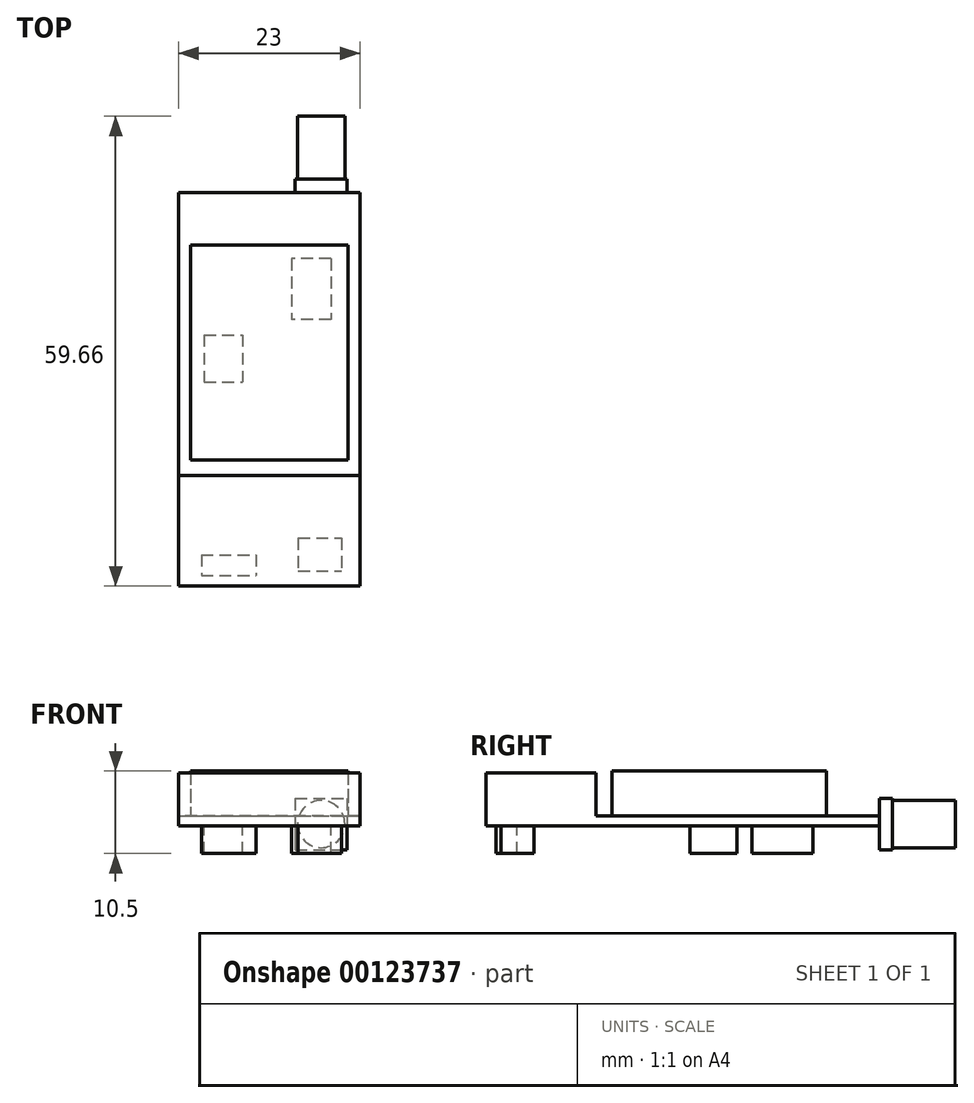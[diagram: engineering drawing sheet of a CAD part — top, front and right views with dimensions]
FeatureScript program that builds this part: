
annotation { "Feature Type Name" : "Feature", "Feature Type Description" : "" }
export const myFeature = defineFeature(function(context is Context, id is Id, definition is map)
    precondition{}
    {
        {
            var Q0;
            Q0=qCreatedBy(makeId("Top.planeOp"),FACE);
            var sketch = newSketch(context, id + "F0", { "sketchPlane" : qUnion([Q0])});
            skLineSegment(sketch, "E0.bottom", {"start": v(-11.5, 25) * mm, "end": v(11.5, 25) * mm});
            skLineSegment(sketch, "E0.top", {"start": v(-11.5, -25) * mm, "end": v(11.5, -25) * mm});
            skLineSegment(sketch, "E0.left", {"start": v(-11.5, 25) * mm, "end": v(-11.5, -25) * mm});
            skLineSegment(sketch, "E0.right", {"start": v(11.5, 25) * mm, "end": v(11.5, -25) * mm});
            skPoint(sketch, "E0.middle", {"position": v(0, 0) * mm});
            skLineSegment(sketch, "E1.bottom", {"start": v(-10, 18.3) * mm, "end": v(10, 18.3) * mm});
            skLineSegment(sketch, "E1.top", {"start": v(-10, -9) * mm, "end": v(10, -9) * mm});
            skLineSegment(sketch, "E1.left", {"start": v(-10, 18.3) * mm, "end": v(-10, -9) * mm});
            skLineSegment(sketch, "E1.right", {"start": v(10, 18.3) * mm, "end": v(10, -9) * mm});
            skPoint(sketch, "E1.middle", {"position": v(0, 4.65) * mm});
            skLineSegment(sketch, "E2", {"start": v(-11.5, -11) * mm, "end": v(11.5, -11) * mm});
            skLineSegment(sketch, "E3", {"start": v(3.3, 25) * mm, "end": v(3.3, 26.66) * mm});
            skLineSegment(sketch, "E4", {"start": v(3.3, 26.66) * mm, "end": v(9.9, 26.66) * mm});
            skLineSegment(sketch, "E5", {"start": v(9.9, 26.66) * mm, "end": v(9.9, 25) * mm});
            skLineSegment(sketch, "E6.bottom", {"start": v(7.85, 16.58) * mm, "end": v(2.83, 16.58) * mm});
            skLineSegment(sketch, "E6.top", {"start": v(7.85, 8.82) * mm, "end": v(2.83, 8.82) * mm});
            skLineSegment(sketch, "E6.left", {"start": v(7.85, 16.58) * mm, "end": v(7.85, 8.82) * mm});
            skLineSegment(sketch, "E6.right", {"start": v(2.83, 16.58) * mm, "end": v(2.83, 8.82) * mm});
            skLineSegment(sketch, "E7.bottom", {"start": v(-8.28, 6.9) * mm, "end": v(-3.38, 6.9) * mm});
            skLineSegment(sketch, "E7.top", {"start": v(-8.28, 0.93) * mm, "end": v(-3.38, 0.93) * mm});
            skLineSegment(sketch, "E7.left", {"start": v(-8.28, 6.9) * mm, "end": v(-8.28, 0.93) * mm});
            skLineSegment(sketch, "E7.right", {"start": v(-3.38, 6.9) * mm, "end": v(-3.38, 0.93) * mm});
            skLineSegment(sketch, "E8.bottom", {"start": v(-8.64, -21.05) * mm, "end": v(-1.7, -21.05) * mm});
            skLineSegment(sketch, "E8.top", {"start": v(-8.64, -23.68) * mm, "end": v(-1.7, -23.68) * mm});
            skLineSegment(sketch, "E8.left", {"start": v(-8.64, -21.05) * mm, "end": v(-8.64, -23.68) * mm});
            skLineSegment(sketch, "E8.right", {"start": v(-1.7, -21.05) * mm, "end": v(-1.7, -23.68) * mm});
            skLineSegment(sketch, "E9.bottom", {"start": v(3.67, -18.9) * mm, "end": v(9.17, -18.9) * mm});
            skLineSegment(sketch, "E9.top", {"start": v(3.67, -23.08) * mm, "end": v(9.17, -23.08) * mm});
            skLineSegment(sketch, "E9.left", {"start": v(3.67, -18.9) * mm, "end": v(3.67, -23.08) * mm});
            skLineSegment(sketch, "E9.right", {"start": v(9.17, -18.9) * mm, "end": v(9.17, -23.08) * mm});
            skSolve(sketch);
        }
        {
            var Q0;
            Q0=makeQuery(id+"F0.imprint","IMPRINT",FACE,{"disambiguationData":[TD([[makeQuery(id+"F0.imprint","IMPRINT",EDGE,{"derivedFrom":sQuery(id+"F0.wireOp",EDGE,"E1.bottom")}),1.0]])]});
            var Q1;
            {var subQ0=sQuery(id+"F0.wireOp",EDGE,"E0.top");Q1=makeQuery(id+"F0.imprint","IMPRINT",FACE,{"disambiguationData":[TD([[makeQuery(id+"F0.imprint","IMPRINT",EDGE,{"derivedFrom":subQ0}),1.0]])]});}
            extrude(context, id + "F1", {"entities" : qUnion([Q0, Q1]), "depth" : 1.3 * mm});
        }
        {
            var Q0;
            Q0=makeQuery(id+"F0.imprint","IMPRINT",FACE,{"disambiguationData":[TD([[makeQuery(id+"F0.imprint","IMPRINT",EDGE,{"derivedFrom":sQuery(id+"F0.wireOp",EDGE,"E1.bottom")}),-1.0]])]});
            var Q1;
            Q1=makeQuery(id+"F0.imprint","IMPRINT",FACE,{"disambiguationData":[TD([[makeQuery(id+"F0.imprint","IMPRINT",EDGE,{"derivedFrom":sQuery(id+"F0.wireOp",EDGE,"E7.bottom")}),-1.0]])]});
            var Q2;
            Q2=makeQuery(id+"F0.imprint","IMPRINT",FACE,{"disambiguationData":[TD([[makeQuery(id+"F0.imprint","IMPRINT",EDGE,{"derivedFrom":sQuery(id+"F0.wireOp",EDGE,"E6.bottom")}),1.0]])]});
            extrude(context, id + "F2", {"entities" : qUnion([Q0, Q1, Q2]), "operationType" : NewBodyOperationType.ADD, "depth" : 7 * mm});
        }
        {
            var Q0;
            {var subQ0=sQuery(id+"F0.wireOp",EDGE,"E0.top");Q0=makeQuery(id+"F0.imprint","IMPRINT",FACE,{"disambiguationData":[TD([[makeQuery(id+"F0.imprint","IMPRINT",EDGE,{"derivedFrom":subQ0}),1.0]])]});}
            var Q1;
            Q1=makeQuery(id+"F0.imprint","IMPRINT",FACE,{"disambiguationData":[TD([[makeQuery(id+"F0.imprint","IMPRINT",EDGE,{"derivedFrom":sQuery(id+"F0.wireOp",EDGE,"E9.bottom")}),-1.0]])]});
            var Q2;
            Q2=makeQuery(id+"F0.imprint","IMPRINT",FACE,{"disambiguationData":[TD([[makeQuery(id+"F0.imprint","IMPRINT",EDGE,{"derivedFrom":sQuery(id+"F0.wireOp",EDGE,"E8.bottom")}),-1.0]])]});
            extrude(context, id + "F3", {"entities" : qUnion([Q0, Q1, Q2]), "operationType" : NewBodyOperationType.ADD, "depth" : 6.75 * mm});
        }
        {
            var Q0;
            {var subQ0=sQuery(id+"F0.wireOp",EDGE,"E3");Q0=makeQuery(id+"F0.imprint","IMPRINT",FACE,{"disambiguationData":[TD([[makeQuery(id+"F0.imprint","IMPRINT",EDGE,{"derivedFrom":subQ0}),-1.0]])]});}
            extrude(context, id + "F4", {"entities" : qUnion([Q0]), "operationType" : NewBodyOperationType.ADD, "depth" : 3.5 * mm, "hasSecondDirection" : true, "secondDirectionOppositeDirection" : true, "secondDirectionDepth" : 3 * mm});
        }
        {
            var Q0;
            Q0=makeQuery(id+"F0.imprint","IMPRINT",FACE,{"disambiguationData":[TD([[makeQuery(id+"F0.imprint","IMPRINT",EDGE,{"derivedFrom":sQuery(id+"F0.wireOp",EDGE,"E6.bottom")}),1.0]])]});
            var Q1;
            Q1=makeQuery(id+"F0.imprint","IMPRINT",FACE,{"disambiguationData":[TD([[makeQuery(id+"F0.imprint","IMPRINT",EDGE,{"derivedFrom":sQuery(id+"F0.wireOp",EDGE,"E7.bottom")}),-1.0]])]});
            var Q2;
            Q2=makeQuery(id+"F0.imprint","IMPRINT",FACE,{"disambiguationData":[TD([[makeQuery(id+"F0.imprint","IMPRINT",EDGE,{"derivedFrom":sQuery(id+"F0.wireOp",EDGE,"E9.bottom")}),-1.0]])]});
            var Q3;
            Q3=makeQuery(id+"F0.imprint","IMPRINT",FACE,{"disambiguationData":[TD([[makeQuery(id+"F0.imprint","IMPRINT",EDGE,{"derivedFrom":sQuery(id+"F0.wireOp",EDGE,"E8.bottom")}),-1.0]])]});
            extrude(context, id + "F5", {"entities" : qUnion([Q0, Q1, Q2, Q3]), "operationType" : NewBodyOperationType.ADD, "oppositeDirection" : true, "depth" : 3.5 * mm});
        }
        {
            var Q0;
            Q0=makeQuery(id+"F4.opExtrude","SWEPT_FACE",FACE,{"disambiguationData":[OSD([sQuery(id+"F0.wireOp",EDGE,"E4")])]});
            var sketch = newSketch(context, id + "F6", { "sketchPlane" : qUnion([Q0])});
            skLineSegment(sketch, "E10", {"start": v(-3.3, 3.5) * mm, "end": v(-9.9, -3) * mm, "construction": true});
            skCircle(sketch, "E11", {"center": v(-6.6, 0.25) * mm, "radius": 3 * mm});
            skSolve(sketch);
        }
        {
            var Q0;
            Q0 = qSketchRegion(id + "F6", true);
            extrude(context, id + "F7", {"entities" : qUnion([Q0]), "operationType" : NewBodyOperationType.ADD, "depth" : 8 * mm});
        }
    });
